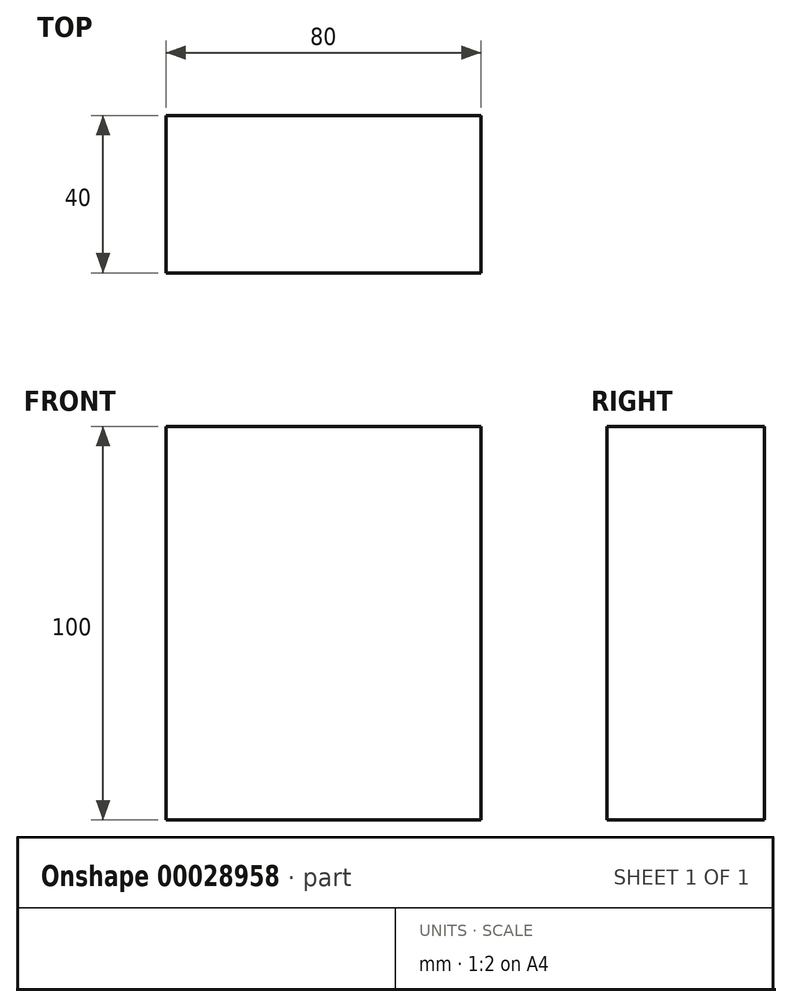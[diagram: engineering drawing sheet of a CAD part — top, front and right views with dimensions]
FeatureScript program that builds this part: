
annotation { "Feature Type Name" : "Feature", "Feature Type Description" : "" }
export const myFeature = defineFeature(function(context is Context, id is Id, definition is map)
    precondition{}
    {
        {
            var Q0;
            Q0=qCreatedBy(makeId("Top.planeOp"),FACE);
            var sketch = newSketch(context, id + "F0", { "sketchPlane" : qUnion([Q0])});
            skLineSegment(sketch, "E0.bottom", {"start": v(-32.37, 6.16) * mm, "end": v(47.63, 6.16) * mm});
            skLineSegment(sketch, "E0.top", {"start": v(-32.37, -33.84) * mm, "end": v(47.63, -33.84) * mm});
            skLineSegment(sketch, "E0.left", {"start": v(-32.37, 6.16) * mm, "end": v(-32.37, -33.84) * mm});
            skLineSegment(sketch, "E0.right", {"start": v(47.63, 6.16) * mm, "end": v(47.63, -33.84) * mm});
            skSolve(sketch);
        }
        {
            var Q0;
            Q0=makeQuery(id+"F0.imprint","IMPRINT",FACE,{"disambiguationData":[TD([[makeQuery(id+"F0.imprint","IMPRINT",EDGE,{"derivedFrom":sQuery(id+"F0.wireOp",EDGE,"E0.bottom")}),-1.0]])]});
            extrude(context, id + "F1", {"entities" : qUnion([Q0]), "depth" : 100 * mm});
        }
    });
